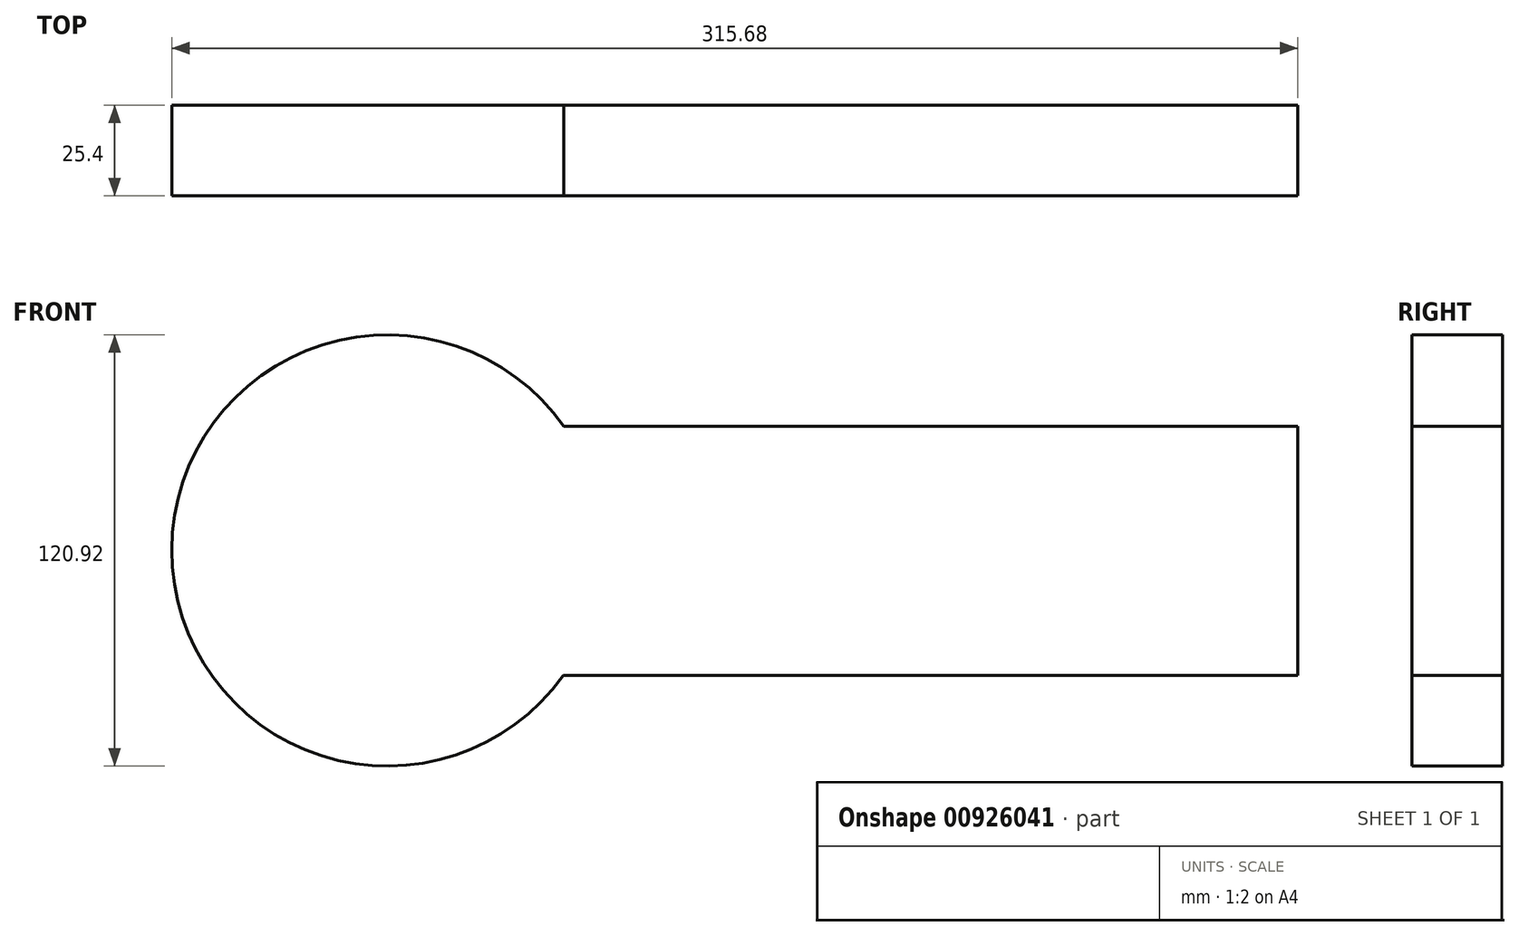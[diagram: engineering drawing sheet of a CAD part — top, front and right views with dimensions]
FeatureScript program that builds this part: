
annotation { "Feature Type Name" : "Feature", "Feature Type Description" : "" }
export const myFeature = defineFeature(function(context is Context, id is Id, definition is map)
    precondition{}
    {
        {
            var Q0;
            Q0=qCreatedBy(makeId("Front.planeOp"),FACE);
            var sketch = newSketch(context, id + "F0", { "sketchPlane" : qUnion([Q0])});
            skCircle(sketch, "E0", {"center": v(-169.12, 35.06) * mm, "radius": 60.46 * mm});
            skLineSegment(sketch, "E1.bottom", {"start": v(-201.65, 69.84) * mm, "end": v(86.1, 69.84) * mm});
            skLineSegment(sketch, "E1.top", {"start": v(-201.65, 0) * mm, "end": v(86.1, 0) * mm});
            skLineSegment(sketch, "E1.left", {"start": v(-201.65, 69.84) * mm, "end": v(-201.65, 0) * mm});
            skLineSegment(sketch, "E1.right", {"start": v(86.1, 69.84) * mm, "end": v(86.1, 0) * mm});
            skSolve(sketch);
        }
        {
            var Q0;
            Q0 = qSketchRegion(id + "F0", true);
            extrude(context, id + "F1", {"entities" : qUnion([Q0]), "depth" : 25.4 * mm, "offsetDistance" : 25.4 * mm});
        }
        {
            var Q0;
            Q0=makeQuery(id+"F1.opExtrude","CAP_FACE",FACE,{"disambiguationData":[OSD([sQuery(id+"F0.wireOp",EDGE,"E0"),sQuery(id+"F0.wireOp",EDGE,"E1.bottom"),sQuery(id+"F0.wireOp",EDGE,"E1.top"),sQuery(id+"F0.wireOp",EDGE,"E1.right")])],"isStart":true});
            extrude(context, id + "F2", {"entities" : qUnion([Q0]), "operationType" : NewBodyOperationType.ADD, "depth" : 25.4 * mm, "offsetDistance" : 25.4 * mm});
        }
        {
            var Q0;
            Q0=makeQuery(id+"F1.opExtrude","CAP_FACE",FACE,{"disambiguationData":[OSD([sQuery(id+"F0.wireOp",EDGE,"E0"),sQuery(id+"F0.wireOp",EDGE,"E1.bottom"),sQuery(id+"F0.wireOp",EDGE,"E1.top"),sQuery(id+"F0.wireOp",EDGE,"E1.right")])],"isStart":false});
            extrude(context, id + "F3", {"entities" : qUnion([Q0]), "operationType" : NewBodyOperationType.REMOVE, "oppositeDirection" : true, "depth" : 25.4 * mm, "offsetDistance" : 25.4 * mm});
        }
    });
